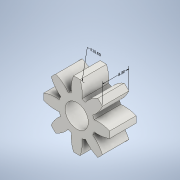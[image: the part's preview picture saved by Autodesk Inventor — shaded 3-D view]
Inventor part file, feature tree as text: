
AUTODESK INVENTOR PART (.ipt)
format: ipt  version: 2022.2 (Build 262287010, 287A)  size: 229,888 bytes
history: native  units: mm (DEFAULTED — no unit token found)
features: other x6, plane x3, sketch x3, extrude x2
ambient origin geometry x8: Origin, YZ Plane, XZ Plane, XY Plane, X Axis, Y Axis, Z Axis, Center Point
bodies: Solid1 (feature_tree)
feature tree (14):
  other  "Annotations"
  extrude  "Extrusion1"  Depth=8.0mm TaperAngle=0.0deg
  plane  "Work Plane2"
  plane  "Work Plane8"
  plane  "Work Plane9"
  other  "Spur Gear"
  extrude  "Extrusion2"  Depth=10.0mm TaperAngle=0.0deg
  sketch  "Sketch1"  dims[d0=20.0mm d1=8.0mm d2=0.0mm]
  sketch  "Sketch2"  dims[d3=16.0mm d4=10.0mm d5=0.0mm]
  other  "Srf1"
  sketch  "Sketch3"  dims[d16=65.0mm d17=0.0mm d34=22.5deg d39=0.0mm d41=0.0mm d43=65.0mm d46=65.0mm d47=0.0mm d48=0.0mm d52=7.0mm d53=0.0mm d54=0.0mm d49=14.089589mm d50=10.0mm d51=8.0mm]
  other  "Pitch Diameter"
  other  "Radial Dimension 1"
  other  "Linear Dimension 1"
